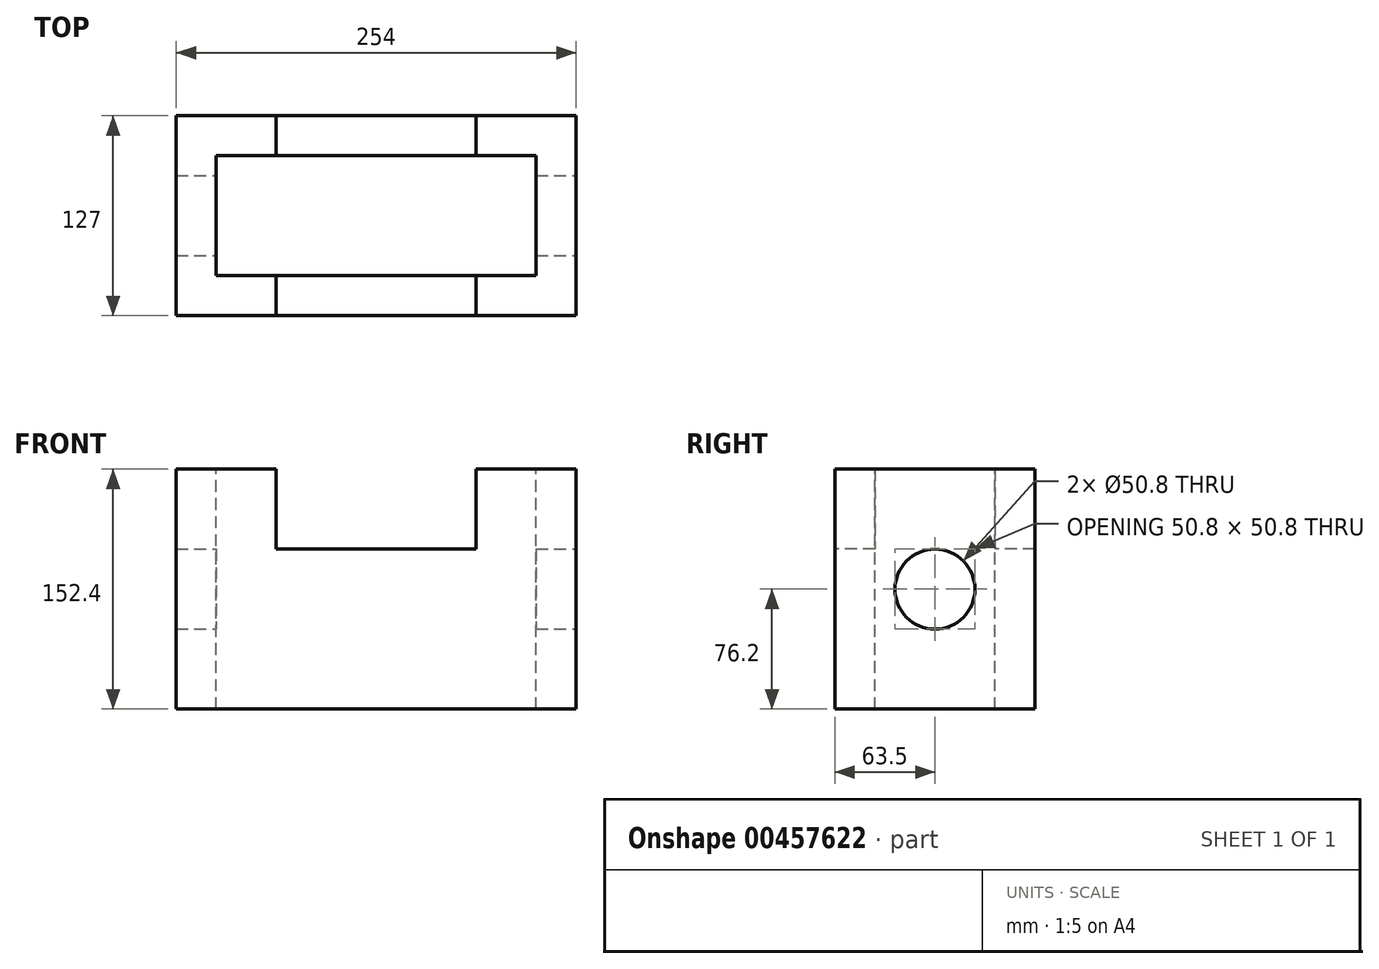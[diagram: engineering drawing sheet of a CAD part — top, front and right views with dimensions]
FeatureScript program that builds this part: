
annotation { "Feature Type Name" : "Feature", "Feature Type Description" : "" }
export const myFeature = defineFeature(function(context is Context, id is Id, definition is map)
    precondition{}
    {
        {
            var Q0;
            Q0=qCreatedBy(makeId("Top.planeOp"),FACE);
            var sketch = newSketch(context, id + "F0", { "sketchPlane" : qUnion([Q0])});
            skLineSegment(sketch, "E0.bottom", {"start": v(-127, 63.5) * mm, "end": v(127, 63.5) * mm});
            skLineSegment(sketch, "E0.top", {"start": v(-127, -63.5) * mm, "end": v(127, -63.5) * mm});
            skLineSegment(sketch, "E0.left", {"start": v(-127, 63.5) * mm, "end": v(-127, -63.5) * mm});
            skLineSegment(sketch, "E0.right", {"start": v(127, 63.5) * mm, "end": v(127, -63.5) * mm});
            skSolve(sketch);
        }
        {
            var Q0;
            Q0 = qSketchRegion(id + "F0", true);
            extrude(context, id + "F1", {"entities" : qUnion([Q0]), "endBound" : BoundingType.SYMMETRIC, "depth" : 152.4 * mm});
        }
        {
            var Q0;
            Q0=makeQuery(id+"F1.opExtrude","CAP_FACE",FACE,{"disambiguationData":[OSD([sQuery(id+"F0.wireOp",EDGE,"E0.bottom"),sQuery(id+"F0.wireOp",EDGE,"E0.top"),sQuery(id+"F0.wireOp",EDGE,"E0.left"),sQuery(id+"F0.wireOp",EDGE,"E0.right")])],"isStart":false});
            var sketch = newSketch(context, id + "F2", { "sketchPlane" : qUnion([Q0])});
            skLineSegment(sketch, "E1.bottom", {"start": v(-101.6, 38.1) * mm, "end": v(101.6, 38.1) * mm});
            skLineSegment(sketch, "E1.top", {"start": v(-101.6, -38.1) * mm, "end": v(101.6, -38.1) * mm});
            skLineSegment(sketch, "E1.left", {"start": v(-101.6, 38.1) * mm, "end": v(-101.6, -38.1) * mm});
            skLineSegment(sketch, "E1.right", {"start": v(101.6, 38.1) * mm, "end": v(101.6, -38.1) * mm});
            skSolve(sketch);
        }
        {
            var Q0;
            Q0 = qSketchRegion(id + "F2", true);
            extrude(context, id + "F3", {"entities" : qUnion([Q0]), "operationType" : NewBodyOperationType.REMOVE, "endBound" : BoundingType.THROUGH_ALL, "oppositeDirection" : true, "depth" : 25.4 * mm});
        }
        {
            var Q0;
            Q0=makeQuery(id+"F1.opExtrude","SWEPT_FACE",FACE,{"disambiguationData":[OSD([sQuery(id+"F0.wireOp",EDGE,"E0.top")])]});
            var sketch = newSketch(context, id + "F4", { "sketchPlane" : qUnion([Q0])});
            skLineSegment(sketch, "E2.bottom", {"start": v(-63.5, 81.14) * mm, "end": v(63.5, 81.14) * mm});
            skLineSegment(sketch, "E2.top", {"start": v(-63.5, 25.4) * mm, "end": v(63.5, 25.4) * mm});
            skLineSegment(sketch, "E2.left", {"start": v(-63.5, 81.14) * mm, "end": v(-63.5, 25.4) * mm});
            skLineSegment(sketch, "E2.right", {"start": v(63.5, 81.14) * mm, "end": v(63.5, 25.4) * mm});
            skSolve(sketch);
        }
        {
            var Q0;
            Q0 = qSketchRegion(id + "F4", true);
            extrude(context, id + "F5", {"entities" : qUnion([Q0]), "operationType" : NewBodyOperationType.REMOVE, "endBound" : BoundingType.THROUGH_ALL, "oppositeDirection" : true, "depth" : 25.4 * mm});
        }
        {
            var Q0;
            Q0=makeQuery(id+"F1.opExtrude","SWEPT_FACE",FACE,{"disambiguationData":[OSD([sQuery(id+"F0.wireOp",EDGE,"E0.right")])]});
            var sketch = newSketch(context, id + "F6", { "sketchPlane" : qUnion([Q0])});
            skCircle(sketch, "E3", {"center": v(0, 0) * mm, "radius": 25.4 * mm});
            skSolve(sketch);
        }
        {
            var Q0;
            Q0 = qSketchRegion(id + "F6", true);
            extrude(context, id + "F7", {"entities" : qUnion([Q0]), "operationType" : NewBodyOperationType.REMOVE, "endBound" : BoundingType.THROUGH_ALL, "oppositeDirection" : true, "depth" : 25.4 * mm});
        }
    });
